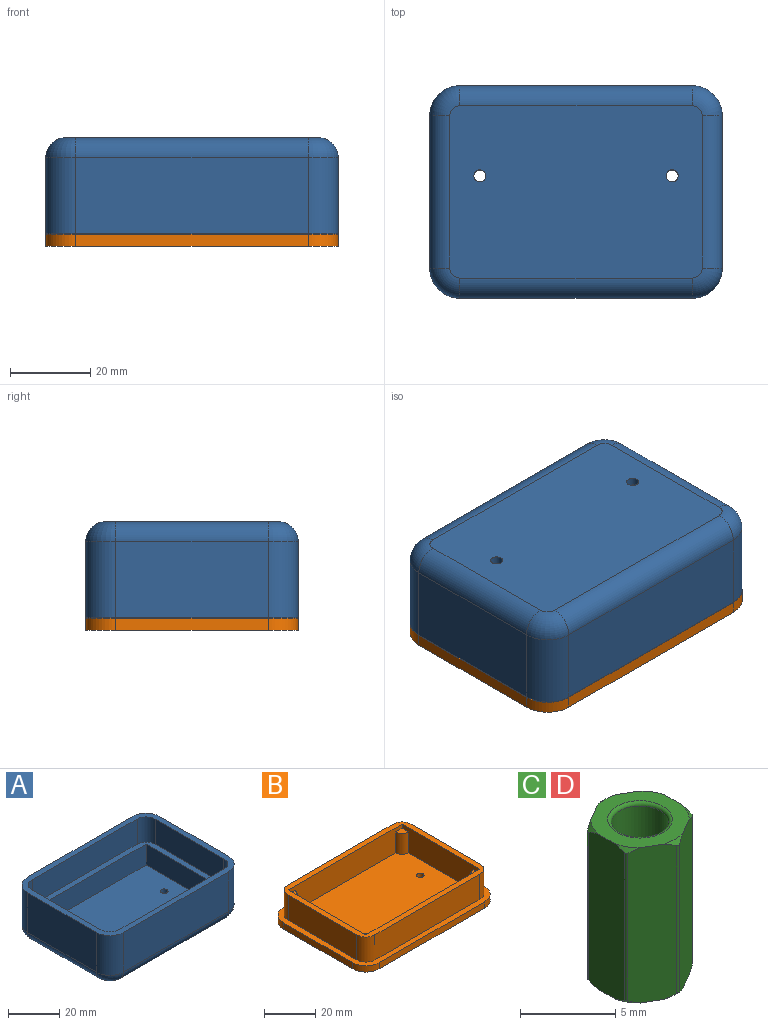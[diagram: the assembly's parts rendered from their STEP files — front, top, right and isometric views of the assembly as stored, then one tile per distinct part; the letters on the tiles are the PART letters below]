
ASSEMBLY  parts=4 mates=6
PART A: 34 faces, bbox 73x53x24 mm
  f0: plane 63x43mm, normal (0,0,1), area 2694.9mm2, adj f8,f10,f12,f13,f14,f15
  f1: plane 58x19mm, normal (0,1,0), area 1102mm2, adj f2,f9,f25,f30
  f2: cylinder r=7.5mm len=19mm, axis (0,0,-1), area 223.8mm2, adj f1,f3,f25,f32
  f3: plane 38x19mm, normal (-1,0,0), area 722mm2, adj f2,f4,f25,f33
  f4: cylinder r=7.5mm len=19mm, axis (0,0,-1), area 223.8mm2, adj f3,f5,f25,f31
  f5: plane 58x19mm, normal (0,-1,0), area 1102mm2, adj f4,f6,f25,f29
  f6: cylinder r=7.5mm len=19mm, axis (0,0,-1), area 223.8mm2, adj f5,f7,f25,f27
  f7: plane 38x19mm, normal (1,0,0), area 722mm2, adj f6,f9,f25,f26
  f8: cylinder r=1.5mm len=3mm, axis (0,0,-1), area 18.8mm2, adj f0,f11
  f9: cylinder r=7.5mm len=19mm, axis (0,0,-1), area 223.8mm2, adj f1,f7,f25,f28
  f10: cylinder r=1.5mm len=3mm, axis (0,0,-1), area 18.8mm2, adj f0,f11
  f11: plane 63x43mm, normal (0,0,-1), area 2689.5mm2, adj f8,f10,f26,f27,f28,f29,f30,f31
  f12: plane 43x10mm, normal (-1,0,0), area 430mm2, adj f0,f13,f15,f16
  f13: plane 63x10mm, normal (0,1,0), area 630mm2, adj f0,f12,f14,f16
  f14: plane 43x10mm, normal (1,0,0), area 430mm2, adj f0,f13,f15,f16
  f15: plane 63x10mm, normal (0,-1,0), area 630mm2, adj f0,f12,f14,f16
  f16: plane 68x48mm, normal (0,0,1), area 533.5mm2, adj f12,f13,f14,f15,f17,f18,f19,f20
  f17: cylinder r=5mm len=12mm, axis (0,0,-1), area 94.2mm2, adj f16,f18,f24,f25
  f18: plane 58x12mm, normal (0,1,0), area 696mm2, adj f16,f17,f19,f25
  f19: cylinder r=5mm len=12mm, axis (0,0,-1), area 94.2mm2, adj f16,f18,f20,f25
  f20: plane 38x12mm, normal (1,0,0), area 456mm2, adj f16,f19,f21,f25
  f21: cylinder r=5mm len=12mm, axis (0,0,-1), area 94.2mm2, adj f16,f20,f22,f25
  f22: plane 58x12mm, normal (0,-1,0), area 696mm2, adj f16,f21,f23,f25
  f23: cylinder r=5mm len=12mm, axis (0,0,-1), area 94.2mm2, adj f16,f22,f24,f25
  f24: plane 38x12mm, normal (-1,0,0), area 456mm2, adj f16,f17,f23,f25
  f25: plane 73x53mm, normal (0,0,1), area 578.2mm2, adj f1,f2,f3,f4,f5,f6,f7,f9
  f26: cylinder r=5mm len=38mm, axis (0,1,0), area 298.5mm2, adj f7,f11,f27,f28
  f27: torus R=2.5mm, axis (0,0,1), area 70.1mm2, adj f6,f11,f26,f29
  f28: torus R=2.5mm, axis (0,0,1), area 70.1mm2, adj f9,f11,f26,f30
  f29: cylinder r=5mm len=58mm, axis (1,0,0), area 455.5mm2, adj f5,f11,f27,f31
  f30: cylinder r=5mm len=58mm, axis (-1,0,0), area 455.5mm2, adj f1,f11,f28,f32
  f31: torus R=2.5mm, axis (0,0,1), area 70.1mm2, adj f4,f11,f29,f33
  f32: torus R=2.5mm, axis (0,0,1), area 70.1mm2, adj f2,f11,f30,f33
  f33: cylinder r=5mm len=38mm, axis (0,-1,0), area 298.5mm2, adj f3,f11,f31,f32
PART B: 34 faces, bbox 73x53x15 mm
  f0: plane 63x12mm, normal (0,1,0), area 686mm2, adj f1,f2,f4,f25,f30,f31,f32,f33
  f1: plane 43x12mm, normal (1,0,0), area 446mm2, adj f0,f2,f3,f25,f28,f29,f32,f33
  f2: plane 63x43mm, normal (0,0,1), area 2656.4mm2, adj f0,f1,f3,f4,f12,f14,f26,f28
  f3: plane 63x12mm, normal (0,-1,0), area 686mm2, adj f1,f2,f4,f25,f26,f27,f28,f29
  f4: plane 43x12mm, normal (-1,0,0), area 446mm2, adj f0,f2,f3,f25,f26,f27,f30,f31
  f5: plane 58x3mm, normal (0,1,0), area 174mm2, adj f6,f13,f15,f16
  f6: cylinder r=7.5mm len=7.5mm, axis (0,0,-1), area 35.3mm2, adj f5,f7,f15,f16
  f7: plane 38x3mm, normal (-1,0,0), area 114mm2, adj f6,f8,f15,f16
  f8: cylinder r=7.5mm len=7.5mm, axis (0,0,-1), area 35.3mm2, adj f7,f9,f15,f16
  f9: plane 58x3mm, normal (0,-1,0), area 174mm2, adj f8,f10,f15,f16
  f10: cylinder r=7.5mm len=7.5mm, axis (0,0,-1), area 35.3mm2, adj f9,f11,f15,f16
  f11: plane 38x3mm, normal (1,0,0), area 114mm2, adj f10,f13,f15,f16
  f12: cylinder r=1.5mm len=3mm, axis (0,0,-1), area 28.3mm2, adj f2,f16
  f13: cylinder r=7.5mm len=7.5mm, axis (0,0,-1), area 35.3mm2, adj f5,f11,f15,f16
  f14: cylinder r=1.5mm len=3mm, axis (0,0,-1), area 28.3mm2, adj f2,f16
  f15: plane 73x53mm, normal (0,0,1), area 578.2mm2, adj f5,f6,f7,f8,f9,f10,f11,f13
  f16: plane 73x53mm, normal (0,0,-1), area 3806.6mm2, adj f5,f6,f7,f8,f9,f10,f11,f12
  f17: plane 58x12mm, normal (0,-1,0), area 696mm2, adj f15,f18,f24,f25
  f18: cylinder r=5mm len=12mm, axis (0,0,-1), area 94.2mm2, adj f15,f17,f19,f25
  f19: plane 38x12mm, normal (1,0,0), area 456mm2, adj f15,f18,f20,f25
  f20: cylinder r=5mm len=12mm, axis (0,0,-1), area 94.2mm2, adj f15,f19,f21,f25
  f21: plane 58x12mm, normal (0,1,0), area 696mm2, adj f15,f20,f22,f25
  f22: cylinder r=5mm len=12mm, axis (0,0,-1), area 94.2mm2, adj f15,f21,f23,f25
  f23: plane 38x12mm, normal (-1,0,0), area 456mm2, adj f15,f22,f24,f25
  f24: cylinder r=5mm len=12mm, axis (0,0,-1), area 94.2mm2, adj f15,f17,f23,f25
  f25: plane 68x48mm, normal (0,0,1), area 533.5mm2, adj f0,f1,f3,f4,f17,f18,f19,f20
  f26: cylinder r=3.5mm len=10mm, axis (0,0,-1), area 55mm2, adj f2,f3,f4,f27
  f27: plane 3.5x3.5mm, normal (0,0,1), area 9.6mm2, adj f3,f4,f26
  f28: cylinder r=3.5mm len=10mm, axis (0,0,-1), area 55mm2, adj f1,f2,f3,f29
  f29: plane 3.5x3.5mm, normal (0,0,1), area 9.6mm2, adj f1,f3,f28
  f30: cylinder r=3.5mm len=10mm, axis (0,0,-1), area 55mm2, adj f0,f2,f4,f31
  f31: plane 3.5x3.5mm, normal (0,0,1), area 9.6mm2, adj f0,f4,f30
  f32: cylinder r=3.5mm len=10mm, axis (0,0,-1), area 55mm2, adj f0,f1,f2,f33
  f33: plane 3.5x3.5mm, normal (0,0,1), area 9.6mm2, adj f0,f1,f32
PART C: 29 faces, bbox 5.5x5.8x10.1 mm
  f0: plane 10.06x2.72mm, normal (1,0,0), area 26.3mm2, adj f6,f7,f11,f13,f21,f22,f23,f28
  f1: plane 10.06x2.36mm, normal (0.5,0.87,0), area 26.3mm2, adj f6,f7,f19,f20,f21,f22,f23,f24
  f2: plane 10.06x2.36mm, normal (-0.5,0.87,0), area 26.3mm2, adj f6,f7,f17,f18,f19,f20,f24,f25
  f3: plane 10.06x2.72mm, normal (-1,0,0), area 26.3mm2, adj f6,f7,f15,f16,f17,f18,f25,f26
  f4: plane 10.06x2.36mm, normal (-0.5,-0.87,0), area 26.3mm2, adj f6,f7,f12,f14,f15,f16,f26,f27
  f5: plane 10.06x2.36mm, normal (0.5,-0.87,0), area 26.3mm2, adj f6,f7,f11,f12,f13,f14,f27,f28
  f6: plane 5.17x5mm, normal (0,0,1), area 11.5mm2, adj f0,f1,f2,f3,f4,f5,f10,f13
  f7: plane 5.17x5mm, normal (0,0,-1), area 11.5mm2, adj f0,f1,f2,f3,f4,f5,f9,f11
  f8: cylinder r=1.5mm len=9.6mm, axis (0,0,1), area 90.5mm2, adj f9,f10
  f9: torus R=1.7mm, axis (0,0,1), area 3.1mm2, adj f7,f8
  f10: torus R=1.7mm, axis (0,0,1), area 3.1mm2, adj f6,f8
  f11: cone r=2.59mm half-angle=45deg, axis (0,0,1), area 0.3mm2, adj f0,f5,f7,f28
  f12: cone r=2.59mm half-angle=45deg, axis (0,0,1), area 0.3mm2, adj f4,f5,f7,f27
  f13: cone r=2.59mm half-angle=45deg, axis (0,0,-1), area 0.3mm2, adj f0,f5,f6,f28
  f14: cone r=2.59mm half-angle=45deg, axis (0,0,-1), area 0.3mm2, adj f4,f5,f6,f27
  f15: cone r=2.59mm half-angle=45deg, axis (0,0,1), area 0.3mm2, adj f3,f4,f7,f26
  f16: cone r=2.59mm half-angle=45deg, axis (0,0,-1), area 0.3mm2, adj f3,f4,f6,f26
  f17: cone r=2.59mm half-angle=45deg, axis (0,0,1), area 0.3mm2, adj f2,f3,f7,f25
  f18: cone r=2.59mm half-angle=45deg, axis (0,0,-1), area 0.3mm2, adj f2,f3,f6,f25
  f19: cone r=2.59mm half-angle=45deg, axis (0,0,1), area 0.3mm2, adj f1,f2,f7,f24
  f20: cone r=2.59mm half-angle=45deg, axis (0,0,-1), area 0.3mm2, adj f1,f2,f6,f24
  f21: cone r=2.59mm half-angle=45deg, axis (0,0,1), area 0.3mm2, adj f0,f1,f7,f23
  f22: cone r=2.59mm half-angle=45deg, axis (0,0,-1), area 0.3mm2, adj f0,f1,f6,f23
  f23: cylinder r=0.2mm len=9.51mm, axis (0,0,-1), area 2mm2, adj f0,f1,f21,f22
  f24: cylinder r=0.2mm len=9.51mm, axis (0,0,-1), area 2mm2, adj f1,f2,f19,f20
  f25: cylinder r=0.2mm len=9.51mm, axis (0,0,-1), area 2mm2, adj f2,f3,f17,f18
  f26: cylinder r=0.2mm len=9.51mm, axis (0,0,-1), area 2mm2, adj f3,f4,f15,f16
  f27: cylinder r=0.2mm len=9.51mm, axis (0,0,-1), area 2mm2, adj f4,f5,f12,f14
  f28: cylinder r=0.2mm len=9.51mm, axis (0,0,-1), area 2mm2, adj f0,f5,f11,f13
PART D: same geometry as C
PLACE A rot(axis=(0,1,0),180deg) t=(-0.03,-0.12,19.45)mm
PLACE B t=(-0.03,-0.12,-7.66)mm fixed
PLACE C t=(23.97,3.88,0.34)mm
PLACE D rot(axis=(0,0,-1),77.1deg) t=(-24.03,3.88,0.34)mm
MATE planar C.f7 <-> B.f2  axis (0,0,-1) through (25.8,5.71,-4.66)mm
MATE planar B.f2 <-> D.f8  axis (0,0,1) through (-0.03,-0.14,-4.66)mm
MATE cylindrical C.f8 <-> A.f8  axis (0,0,1) through (23.97,3.88,5.34)mm
MATE cylindrical B.f14 <-> C.f8  axis (0,0,1) through (23.97,3.88,-4.66)mm
MATE cylindrical D.f8 <-> A.f10  axis (0,0,1) through (-24.03,3.88,5.34)mm
MATE cylindrical D.f8 <-> B.f12  axis (0,0,-1) through (-24.03,3.88,-4.66)mm
